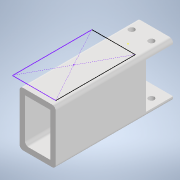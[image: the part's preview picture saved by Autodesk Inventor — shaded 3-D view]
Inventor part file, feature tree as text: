
AUTODESK INVENTOR PART (.ipt)
format: ipt  version: 2021 (Build 250183000, 183)  size: 218,624 bytes
history: native  units: mm
features: sketch x10, extrude x8, other x4, fillet x2, reference x2, shell x1, mirror x1
ambient origin geometry x8: Origin, YZ Plane, XZ Plane, XY Plane, X Axis, Y Axis, Z Axis, Center Point
bodies: Solid1 (feature_tree)
feature tree (28):
  extrude  "Extrusion1"  Depth=30.0mm
  shell  "Shell1"  Thickness=50.0mm
  sketch  "Sketch2"  dims[d4=3.0mm d5=2.5mm]
  extrude  "Extrusion2"  Depth=2.5mm
  sketch  "Sketch4"  dims[d16=2.0mm d17=5.0mm]
  extrude  "Extrusion4"  Depth=15.0mm TaperAngle=0.0deg
  fillet  "Fillet1"  [1 undecoded]
  fillet  "Fillet2"  Radius=2.0mm
  extrude  "Extrusion5"  Depth=5.0mm
  extrude  "Extrusion6"  Depth=1.0mm
  extrude  "Extrusion7"  Depth=30.0mm TaperAngle=0.0deg
  extrude  "Extrusion8"  Depth=5.0mm TaperAngle=0.0deg
  extrude  "Extrusion9"  [1 undecoded]
  mirror  "Mirror1"
  sketch  "Sketch1"  dims[d0=20.0mm d1=30.0mm d2=50.0mm d3=0.0mm]
  sketch  "Sketch3"  dims[d6=2.5mm d7=15.0mm d8=0.0mm d13=0.0mm d14=0.0mm d15=2.0mm]
  sketch  "Sketch6"  dims[d18=10.0mm d19=0.0mm d20=1.0mm]
  reference  "Reference1"
  reference  "Reference2"
  sketch  "Sketch7"  dims[d21=30.0mm d22=0.0mm d23=30.0mm d24=0.0mm]
  sketch  "Sketch8"  dims[d25=5.0mm d26=0.0mm d27=6.25mm d28=0.0mm]
  sketch  "Sketch9"
  sketch  "Sketch10"
  sketch  "Sketch11"
  parser-record x1  (decoder bookkeeping rows leaked as tree rows — omitted from the tree; the rows remain in map.json)
  other  "whole_assembly.iam"
  other  "tool_holder:1"
  other  "Part3:1"
note: 2 required parameter values undecoded (feature->parameter linkage not recoverable at this tier; creation-order binding heuristic only, values carry confidence <= 0.55)
note: 1 file-system path scrubbed to <path> (originals preserved in map.json)
